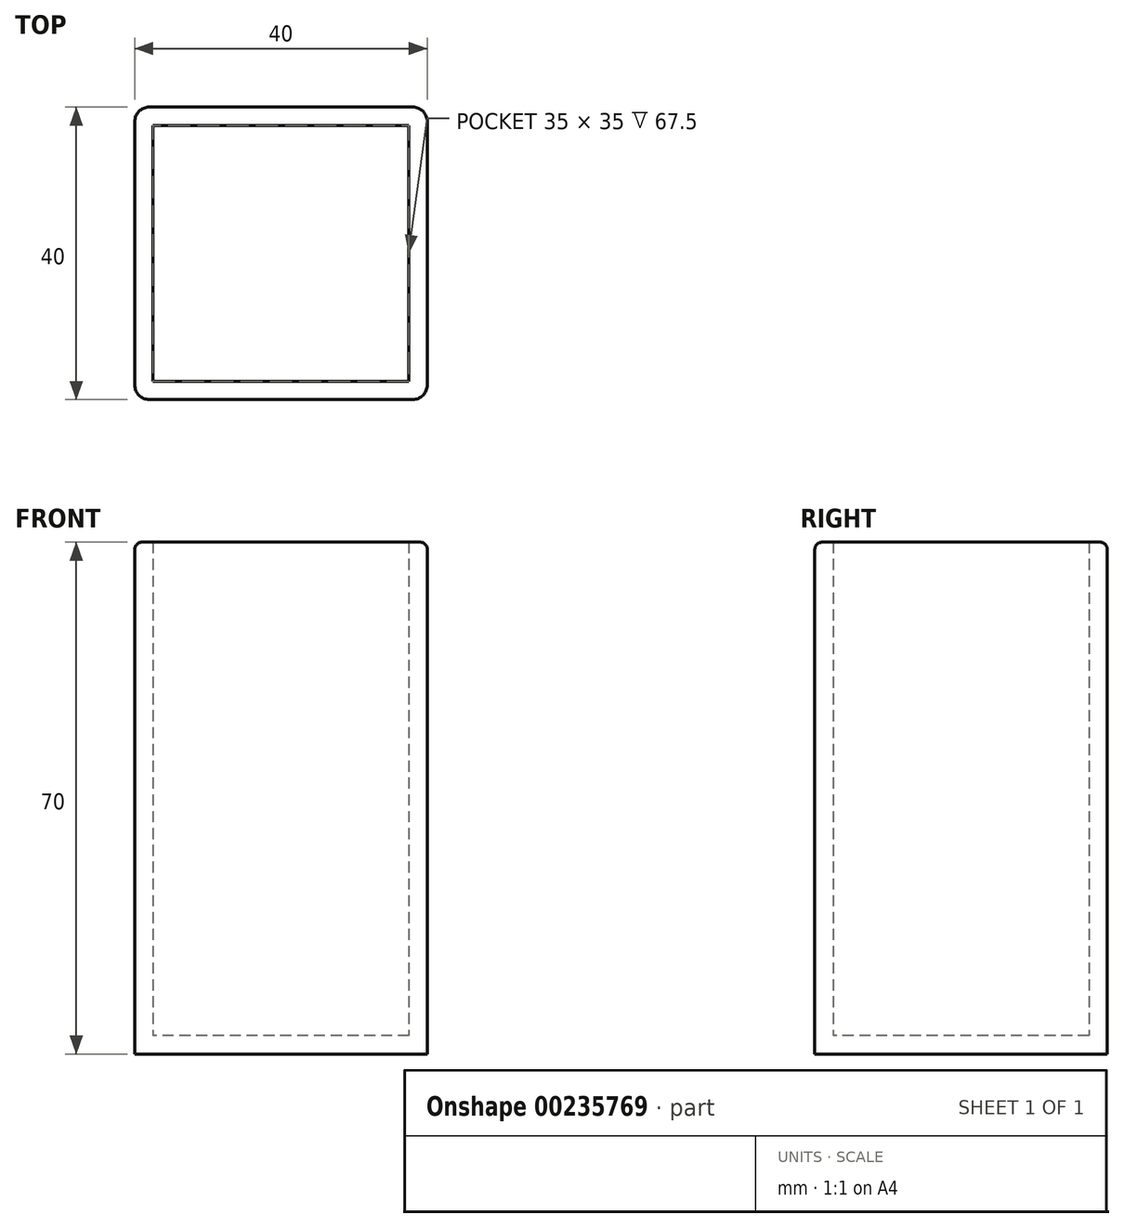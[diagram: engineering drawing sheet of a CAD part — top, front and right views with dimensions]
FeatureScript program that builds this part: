
annotation { "Feature Type Name" : "Feature", "Feature Type Description" : "" }
export const myFeature = defineFeature(function(context is Context, id is Id, definition is map)
    precondition{}
    {
        {
            var Q0;
            Q0=qCreatedBy(makeId("Top.planeOp"),FACE);
            var sketch = newSketch(context, id + "F0", { "sketchPlane" : qUnion([Q0])});
            skLineSegment(sketch, "E0.bottom", {"start": v(18, 20) * mm, "end": v(-18, 20) * mm});
            skLineSegment(sketch, "E0.top", {"start": v(18, -20) * mm, "end": v(-18, -20) * mm});
            skLineSegment(sketch, "E0.left", {"start": v(20, 18) * mm, "end": v(20, -18) * mm});
            skLineSegment(sketch, "E0.right", {"start": v(-20, 18) * mm, "end": v(-20, -18) * mm});
            skPoint(sketch, "E0.middle", {"position": v(0, 0) * mm});
            skPoint(sketch, "E1.visualSharp", {"position": v(-20, 20) * mm});
            skArc(sketch, "E1.filletArc", {"start": v(-18, 20) * mm, "mid": v(-19.41, 19.41) * mm, "end": v(-20, 18) * mm});
            skPoint(sketch, "E2.visualSharp", {"position": v(20, 20) * mm});
            skArc(sketch, "E2.filletArc", {"start": v(20, 18) * mm, "mid": v(19.41, 19.41) * mm, "end": v(18, 20) * mm});
            skPoint(sketch, "E3.visualSharp", {"position": v(20, -20) * mm});
            skArc(sketch, "E3.filletArc", {"start": v(18, -20) * mm, "mid": v(19.41, -19.41) * mm, "end": v(20, -18) * mm});
            skPoint(sketch, "E4.visualSharp", {"position": v(-20, -20) * mm});
            skArc(sketch, "E4.filletArc", {"start": v(-20, -18) * mm, "mid": v(-19.41, -19.41) * mm, "end": v(-18, -20) * mm});
            skSolve(sketch);
        }
        {
            var Q0;
            Q0=makeQuery(id+"F0.imprint","IMPRINT",FACE,{"disambiguationData":[TD([[makeQuery(id+"F0.imprint","IMPRINT",EDGE,{"derivedFrom":sQuery(id+"F0.wireOp",EDGE,"E0.bottom")}),1.0]])]});
            extrude(context, id + "F1", {"entities" : qUnion([Q0]), "depth" : 70 * mm});
        }
        {
            var Q0;
            Q0=makeQuery(id+"F1.opExtrude","CAP_FACE",FACE,{"disambiguationData":[OSD([sQuery(id+"F0.wireOp",EDGE,"E0.bottom"),sQuery(id+"F0.wireOp",EDGE,"E0.top"),sQuery(id+"F0.wireOp",EDGE,"E0.left"),sQuery(id+"F0.wireOp",EDGE,"E0.right"),sQuery(id+"F0.wireOp",EDGE,"E1.filletArc"),sQuery(id+"F0.wireOp",EDGE,"E2.filletArc"),sQuery(id+"F0.wireOp",EDGE,"E3.filletArc"),sQuery(id+"F0.wireOp",EDGE,"E4.filletArc")])],"isStart":false});
            shell(context, id + "F2", {"entities" : qUnion([Q0]), "thickness" : 2.5 * mm});
        }
        {
            var Q0;
            Q0=makeQuery(id+"F1.opExtrude","CAP_EDGE",EDGE,{"disambiguationData":[OSD([sQuery(id+"F0.wireOp",EDGE,"E0.top")])],"isStart":false});
            fillet(context, id + "F3", {"entities" : qUnion([Q0]), "radius" : 1 * mm, "tangentPropagation" : true, "allowEdgeOverflow" : false});
        }
        {
            var Q0;
            Q0=makeQuery(id+"F1.opExtrude","SWEPT_FACE",FACE,{"disambiguationData":[OSD([sQuery(id+"F0.wireOp",EDGE,"E0.top")])]});
            var sketch = newSketch(context, id + "F4", { "sketchPlane" : qUnion([Q0])});
            skFitSpline(sketch, "E5", {"points": [v(-5.7, 48.02) * mm, v(-8.18, 48.07) * mm, v(-14.4, 49.68) * mm, v(-14.89, 53.28) * mm, v(-11.41, 54.53) * mm, v(-9.92, 56.76) * mm, v(-6.57, 57.26) * mm, v(-5.52, 50.6) * mm, v(-5.7, 48.02) * mm]});
            skFitSpline(sketch, "E6.MirrorC", {"points": [v(-5.84, 47.46) * mm, v(-8.18, 47.36) * mm, v(-14.4, 45.74) * mm, v(-14.89, 42.14) * mm, v(-11.41, 40.9) * mm, v(-9.92, 38.66) * mm, v(-6.57, 38.17) * mm, v(-5.59, 45.37) * mm, v(-5.84, 47.46) * mm]});
            skFitSpline(sketch, "E7.MirrorC", {"points": [v(-4.89, 48.02) * mm, v(-2.67, 47.97) * mm, v(3.67, 49.68) * mm, v(4.17, 53.28) * mm, v(0.7, 54.53) * mm, v(-0.8, 56.76) * mm, v(-4.15, 57.26) * mm, v(-5.08, 49.72) * mm, v(-4.89, 48.02) * mm]});
            skFitSpline(sketch, "E8.MirrorC", {"points": [v(-5.1, 47.28) * mm, v(-2.89, 47.38) * mm, v(3.67, 45.74) * mm, v(4.17, 42.14) * mm, v(0.7, 40.9) * mm, v(-0.8, 38.66) * mm, v(-4.15, 38.17) * mm, v(-5.24, 45.23) * mm, v(-5.1, 47.28) * mm]});
            skFitSpline(sketch, "E9", {"points": [v(6.05, 29.25) * mm, v(5.3, 29.9) * mm, v(3.1, 33.52) * mm, v(4.74, 34.61) * mm, v(6.46, 33.6) * mm, v(7.56, 34.61) * mm, v(9.36, 33.28) * mm, v(7.05, 30.2) * mm, v(6.05, 29.25) * mm]});
            skFitSpline(sketch, "E10.MirrorC", {"points": [v(6.38, 29.11) * mm, v(6.87, 28.42) * mm, v(10.56, 26.06) * mm, v(11.65, 27.7) * mm, v(10.64, 29.42) * mm, v(11.65, 30.52) * mm, v(10.32, 32.32) * mm, v(7.36, 30.12) * mm, v(6.38, 29.11) * mm]});
            skFitSpline(sketch, "E11.MirrorC", {"points": [v(6.1, 28.84) * mm, v(6.71, 28.23) * mm, v(9.02, 24.52) * mm, v(7.38, 23.43) * mm, v(5.66, 24.44) * mm, v(4.56, 23.43) * mm, v(2.76, 24.76) * mm, v(4.12, 26.89) * mm, v(6.1, 28.84) * mm]});
            skFitSpline(sketch, "E12.MirrorC", {"points": [v(5.77, 29.06) * mm, v(5.18, 29.6) * mm, v(1.56, 31.98) * mm, v(0.47, 30.34) * mm, v(1.48, 28.61) * mm, v(0.47, 27.52) * mm, v(1.8, 25.72) * mm, v(5.25, 28.45) * mm, v(5.77, 29.06) * mm]});
            skFitSpline(sketch, "E13", {"points": [v(-8.86, 10.3) * mm, v(-10.41, 10.4) * mm, v(-15.72, 11.62) * mm, v(-15.3, 14.48) * mm, v(-12.79, 14.76) * mm, v(-12.72, 16.72) * mm, v(-9.65, 16.86) * mm, v(-8.84, 11.93) * mm, v(-8.86, 10.3) * mm]});
            skFitSpline(sketch, "E14.MirrorC", {"points": [v(-8.31, 10.42) * mm, v(-6.48, 10.22) * mm, v(-1.47, 10.62) * mm, v(-1.49, 13.52) * mm, v(-3.94, 14.14) * mm, v(-3.73, 16.09) * mm, v(-6.76, 16.65) * mm, v(-8.38, 11.36) * mm, v(-8.31, 10.42) * mm]});
            skFitSpline(sketch, "E15.MirrorC", {"points": [v(-8.38, 9.96) * mm, v(-6.96, 9.88) * mm, v(-1.6, 8.63) * mm, v(-2.03, 5.76) * mm, v(-4.54, 5.48) * mm, v(-4.61, 3.53) * mm, v(-7.68, 3.4) * mm, v(-8.53, 8.17) * mm, v(-8.38, 9.96) * mm]});
            skFitSpline(sketch, "E16.MirrorC", {"points": [v(-8.92, 9.83) * mm, v(-10.34, 10.08) * mm, v(-15.86, 9.62) * mm, v(-15.84, 6.73) * mm, v(-13.4, 6.1) * mm, v(-13.6, 4.16) * mm, v(-10.57, 3.6) * mm, v(-8.9, 8.5) * mm, v(-8.92, 9.83) * mm]});
            skSolve(sketch);
        }
        {
            var Q0;
            Q0=qCreatedBy(makeId("Right.planeOp"),FACE);
            cPlane(context, id + "F5", {"entities" : qUnion([Q0]), "cplaneType" : CPlaneType.OFFSET, "offset" : 6 * mm, "width" : 150 * mm, "height" : 150 * mm});
        }
    });
